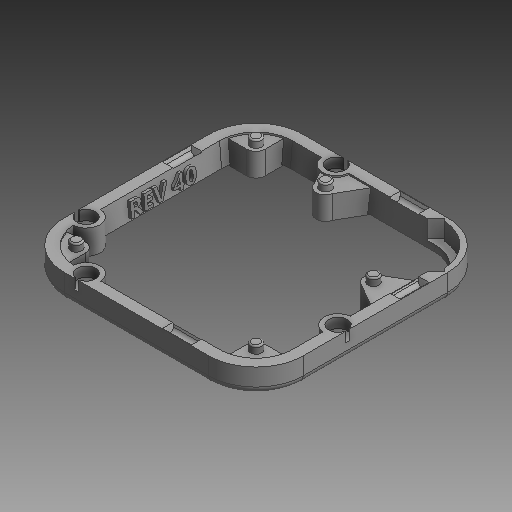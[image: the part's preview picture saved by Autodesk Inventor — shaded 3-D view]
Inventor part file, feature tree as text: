
AUTODESK INVENTOR PART (.ipt)
format: ipt  version: 2018 (Build 220112000, 112)  size: 4,837,888 bytes
history: native  units: in
note: dims shown in document units (in); Inventor stores cm internally (conversion verified against a paired STEP export)
features: other x17, extrude x17, sketch x9, fillet x5, plane x4, pattern_circular x2, mirror x2, move_body x1, thicken_offset x1
ambient origin geometry x8: Origin, YZ Plane, XZ Plane, XY Plane, X Axis, Y Axis, Z Axis, Center Point
bodies: Solid12 (feature_tree), Solid22 (feature_tree), Solid23 (feature_tree), Solid24 (feature_tree), Solid25 (feature_tree), Solid26 (feature_tree), Solid28 (feature_tree), Solid1 (feature_tree), Solid32 (feature_tree)
feature tree (58):
  other  "Remote Shell.ipt"
  other  "Eagle PCB rev 38.ipt"
  plane  "Work Plane15"
  other  "PCB Bottom Plane"
  other  "Top Plane"
  move_body  "Move Body3"
  extrude  "Extrusion33"  Depth=0.3937in
  other  "Mounts Sketch"
  extrude  "Extrusion2"  Depth=0.05in TaperAngle=0.0deg
  fillet  "Fillet5"  Radius=0.025in
  fillet  "Fillet10"  Radius=0.025in
  extrude  "Extrusion37"  Depth=0.078in
  other  "Work Axis1"
  other  "Lip Plane"
  other  "Magnet Bottom Plane"
  other  "Bottom Plane"
  extrude  "Logo Extrusion"  Depth=0.078in
  plane  "Work Plane18"
  sketch  "Sketch28"  dims[d28=0.078in d29=0.078in]
  extrude  "Extrusion24"  TaperAngle=0.0deg  [1 undecoded]
  other  "Magnet Sketch"
  extrude  "Magnet Holder"  Depth=0.129in
  extrude  "Magnet Cut"  Depth=0.01in
  extrude  "Mating Extrusion"  Depth=0.125in
  fillet  "Fillet9"  Radius=0.25in
  pattern_circular  "Circular Pattern8"  [2 undecoded]
  mirror  "Mirror3"
  mirror  "Mirror4"
  extrude  "Extrusion25"  Depth=0.3937in
  extrude  "Extrusion28"  Depth=0.3937in
  pattern_circular  "Circular Pattern11"  [2 undecoded]
  extrude  "Extrusion30"  Depth=0.3937in
  extrude  "Extrusion34"  Depth=0.3937in
  extrude  "Extrusion35"  Depth=0.3937in
  fillet  "Fillet14"  Radius=1.0in
  plane  "Work Plane17"
  extrude  "Extrusion36"  Depth=0.3937in
  extrude  "Extrusion38"  Depth=0.3937in
  extrude  "Extrusion39"  Depth=0.3937in TaperAngle=360.0deg
  extrude  "Extrusion40"  TaperAngle=90.0deg  [1 undecoded]
  thicken_offset  "Thicken1"
  fillet  "Fillet16"  Radius=0.05in
  other  "Bottom Solid::Remote Shell.ipt"
  other  "TaggingFeature1"
  sketch  "Sketch7"  dims[d0=0.3937in d1=0.22in]
  sketch  "Sketch21"  dims[d2=0.025in d5=0.05in d6=0.0in d7=0.025in d8=0.025in]
  plane  "Work Plane14"
  sketch  "Sketch31"  dims[d30=0.025in d31=0.078in]
  other  "Pattern of Solid23:16"
  other  "Pattern of Solid23:17"
  other  "Pattern of Solid23:18"
  sketch  "Sketch32"  dims[d32=0.078in d58=0.0in d67=-0.0675in]
  sketch  "Sketch34"  dims[d78=0.02in d79=0.0in d101=0.129in]
  sketch  "Sketch35"  dims[d103=0.03in d104=0.0206in d132=0.01in]
  sketch  "Sketch36"  dims[d151=0.068in d152=0.0in d154=0.125in d155=0.25in]
  sketch  "Sketch39"  dims[d156=0.15in d159=0.025in d160=0.175in d161=-0.2199in d168=0.0312in d184=0.078in d185=0.025in d192=0.01in d196=1.0in d197=0.0344in d198=1.0in d199=0.0in d200=0.075in d201=0.15in d202=1.5748in d203=360.0deg d205=90.0deg d209=0.05in d210=0.035in d224=0.19in d225=0.015in d226=0.03in d227=0.0625in d228=30.0deg d229=1.5748in d230=360.0deg d232=45.0deg d233=0.15in d234=0.45in d237=45.0deg d238=0.12in d239=0.0in d252=1.05in d253=1.05in d254=1.0in d255=0.0in d256=0.375in d257=0.02in d258=0.0in d259=0.02in d260=0.0in d261=0.025in d264=0.0in d265=0.0in d266=1.0in d267=0.0in d268=120.0deg d269=60.0deg d270=30.0deg d271=30.0deg d282=0.129in d283=0.05in d284=0.035in d285=0.19in d286=0.129in d287=0.05in d288=0.035in d289=0.19in d290=0.129in d291=0.05in d292=0.035in d293=0.19in d298=0.01in d299=0.03in d300=0.05in d301=0.3937in d302=0.0in d303=0.295in d304=0.0in d305=0.0in d306=0.0in d307=0.068in d308=0.0in d309=0.068in d310=0.0in d311=0.03in d312=0.01in d313=0.01in d314=0.03in d315=0.01in d316=0.03in d317=0.01in d318=0.03in]
  other  "Solid1::Eagle PCB rev 38.ipt"
  other  "TaggingFeature6"
note: 6 required parameter values undecoded (feature->parameter linkage not recoverable at this tier; creation-order binding heuristic only, values carry confidence <= 0.55)
